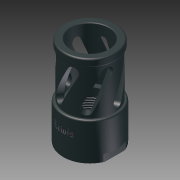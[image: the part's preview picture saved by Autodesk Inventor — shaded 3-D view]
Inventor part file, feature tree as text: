
AUTODESK INVENTOR PART (.ipt)
format: ipt  version: 2011 (Build 150239000, 239)  size: 1,820,672 bytes
history: native  units: in
note: dims shown in document units (in); Inventor stores cm internally (conversion verified against a paired STEP export)
features: sketch x6, fillet x3, plane x3, extrude x2, emboss x2, projected_geometry x2, revolve x1, thread x1, chamfer x1, pattern_circular x1, other x1
ambient origin geometry x8: Origin, YZ Plane, XZ Plane, XY Plane, X Axis, Y Axis, Z Axis, Center Point
bodies: Solid1 (feature_tree)
feature tree (23):
  revolve  "Revolution1"  [1 undecoded]
  thread  "Thread1"  [1 undecoded]
  fillet  "Fillet1"  Radius=0.175in
  plane  "Work Plane1"
  extrude  "Extrusion1"  Depth=0.2in
  plane  "Work Plane2"
  sketch  "Sketch4"  dims[d7=0.75in d8=90.0deg d9=0.5in d10=0.0in d11=0.025in]
  extrude  "Extrusion3"  TaperAngle=90.0deg  [1 undecoded]
  fillet  "Fillet3"  Radius=0.5in
  fillet  "Fillet4"  Radius=0.025in
  chamfer  "Chamfer1"  Distance=0.04in
  sketch  "3D Sketch2"
  emboss  "Emboss1"
  pattern_circular  "Circular Pattern2"  [2 undecoded]
  plane  "Work Plane4"
  emboss  "Emboss3"
  sketch  "Sketch1"  dims[d0=1.5in d1=0.465in d2=1.5in d4=0.175in]
  sketch  "Sketch2"  dims[d5=0.625in d6=0.2in]
  projected_geometry  "Projected Loop1"
  projected_geometry  "Projected Loop2"
  sketch  "Sketch5"  dims[d12=0.9in]
  other  "Project to Surface1"
  sketch  "Sketch9"  dims[d13=0.82in d14=0.04in d15=0.125in d16=0.125in d17=1.0in d18=0.0in d28=0.625in d29=0.875in d30=0.0in d32=0.015in d33=0.015in d34=0.05in d35=0.125in d36=45.0deg d41=0.16in d42=0.16in d43=0.125in d44=0.125in d45=0.1in d46=0.0in d47=2.3622in d48=360.0deg d52=0.02in d53=0.0in]
note: 5 required parameter values undecoded (feature->parameter linkage not recoverable at this tier; creation-order binding heuristic only, values carry confidence <= 0.55)